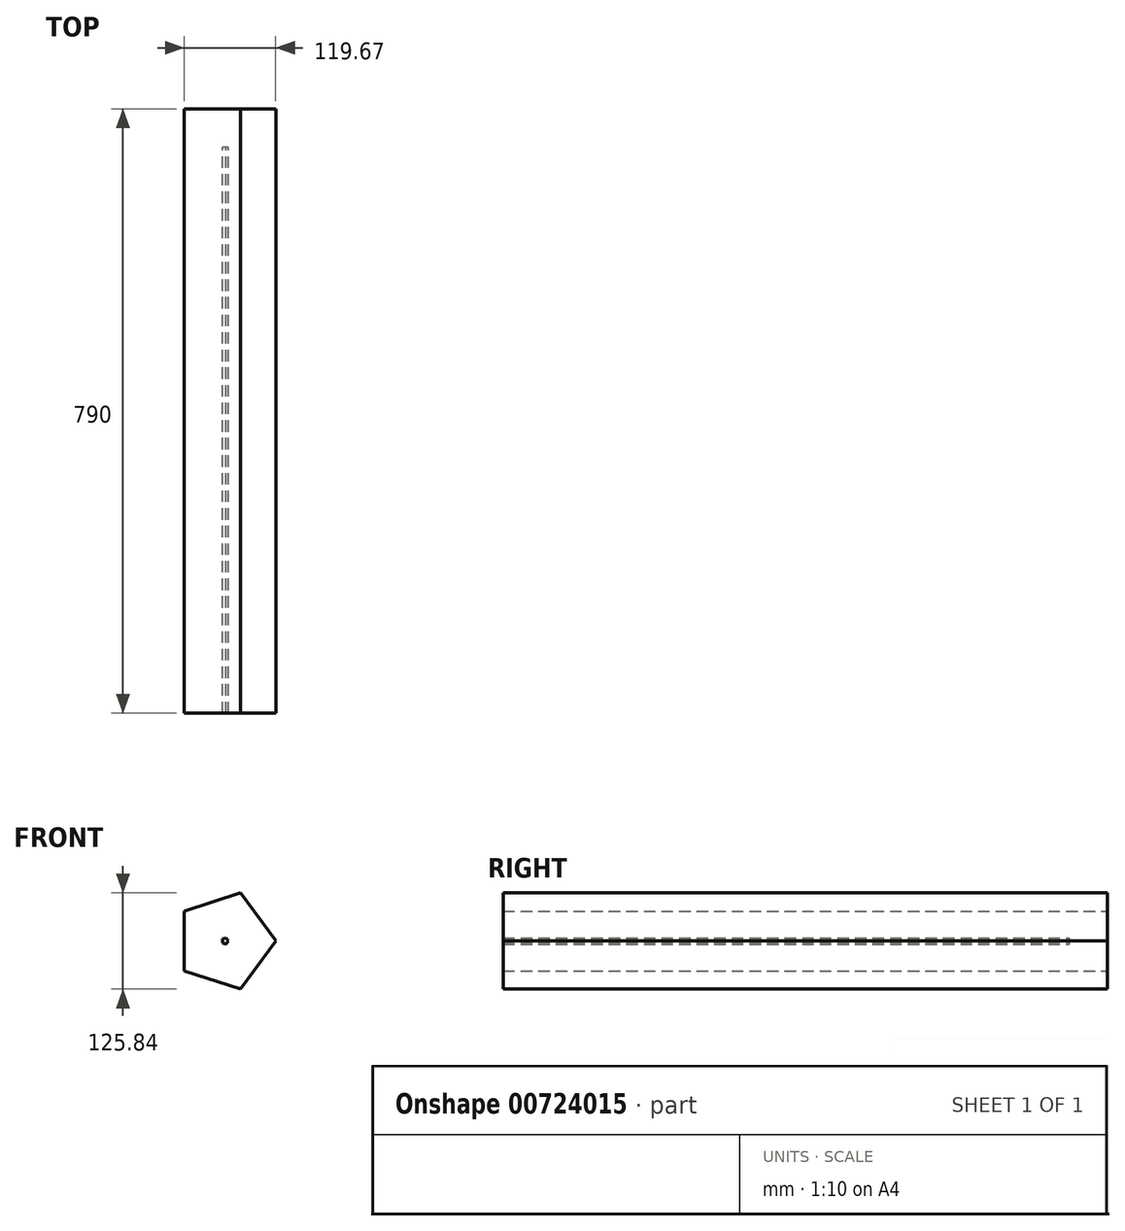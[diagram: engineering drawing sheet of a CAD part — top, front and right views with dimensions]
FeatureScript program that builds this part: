
annotation { "Feature Type Name" : "Feature", "Feature Type Description" : "" }
export const myFeature = defineFeature(function(context is Context, id is Id, definition is map)
    precondition{}
    {
        {
            var Q0;
            Q0=qCreatedBy(makeId("Front.planeOp"),FACE);
            var sketch = newSketch(context, id + "F0", { "sketchPlane" : qUnion([Q0])});
            skCircle(sketch, "E0.cCircle", {"center": v(0, 0) * mm, "radius": 53.52 * mm, "construction": true});
            skLineSegment(sketch, "E0.0", {"start": v(-53.52, -38.88) * mm, "end": v(-53.52, 38.88) * mm});
            skLineSegment(sketch, "E0.1", {"start": v(-53.52, 38.88) * mm, "end": v(20.44, 62.92) * mm});
            skLineSegment(sketch, "E0.2", {"start": v(20.44, 62.92) * mm, "end": v(66.15, 0) * mm});
            skLineSegment(sketch, "E0.3", {"start": v(66.15, 0) * mm, "end": v(20.44, -62.92) * mm});
            skLineSegment(sketch, "E0.4", {"start": v(20.44, -62.92) * mm, "end": v(-53.52, -38.88) * mm});
            skPoint(sketch, "E0.0.midPoint", {"position": v(-53.52, 0) * mm});
            skSolve(sketch);
        }
        {
            var Q0;
            Q0 = qSketchRegion(id + "F0", true);
            extrude(context, id + "F1", {"entities" : qUnion([Q0]), "depth" : 790 * mm, "offsetDistance" : 25 * mm});
        }
        {
            var Q0;
            Q0=makeQuery(id+"F1.opExtrude","CAP_FACE",FACE,{"disambiguationData":[OSD([sQuery(id+"F0.wireOp",EDGE,"E0.0"),sQuery(id+"F0.wireOp",EDGE,"E0.1"),sQuery(id+"F0.wireOp",EDGE,"E0.2"),sQuery(id+"F0.wireOp",EDGE,"E0.3"),sQuery(id+"F0.wireOp",EDGE,"E0.4")])],"isStart":false});
            shell(context, id + "F2", {"entities" : qUnion([Q0]), "thickness" : 50 * mm});
        }
    });
